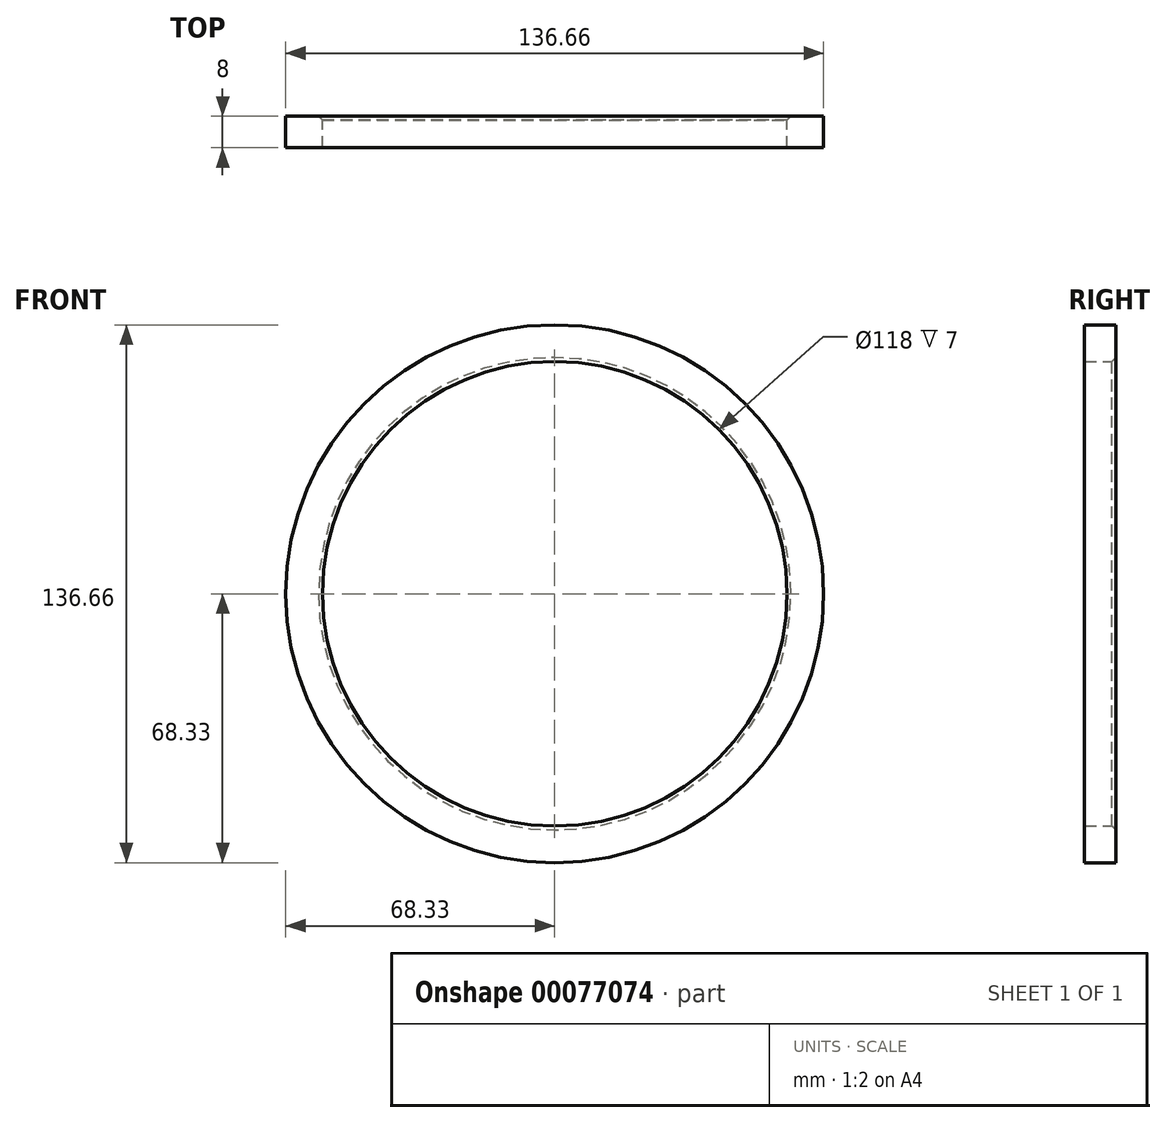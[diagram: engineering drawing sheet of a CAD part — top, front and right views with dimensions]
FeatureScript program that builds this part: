
annotation { "Feature Type Name" : "Feature", "Feature Type Description" : "" }
export const myFeature = defineFeature(function(context is Context, id is Id, definition is map)
    precondition{}
    {
        {
            var Q0;
            Q0=qCreatedBy(makeId("Front.planeOp"),FACE);
            var sketch = newSketch(context, id + "F0", { "sketchPlane" : qUnion([Q0])});
            skCircle(sketch, "E0", {"center": v(0, 0) * mm, "radius": 68.33 * mm});
            skCircle(sketch, "E1", {"center": v(0, 0) * mm, "radius": 59 * mm});
            skSolve(sketch);
        }
        {
            var Q0;
            Q0=makeQuery(id+"F0.imprint","IMPRINT",FACE,{"disambiguationData":[TD([[makeQuery(id+"F0.imprint","IMPRINT",EDGE,{"derivedFrom":sQuery(id+"F0.wireOp",EDGE,"E0")}),1.0]])]});
            extrude(context, id + "F1", {"entities" : qUnion([Q0]), "depth" : 8 * mm, "offsetDistance" : 25 * mm});
        }
        {
            var Q0;
            Q0=makeQuery(id+"F1.opExtrude","CAP_EDGE",EDGE,{"disambiguationData":[OSD([sQuery(id+"F0.wireOp",EDGE,"E1")])],"isStart":true});
            chamfer(context, id + "F2", {"entities" : qUnion([Q0]), "width" : 1 * mm, "tangentPropagation" : true});
        }
    });
